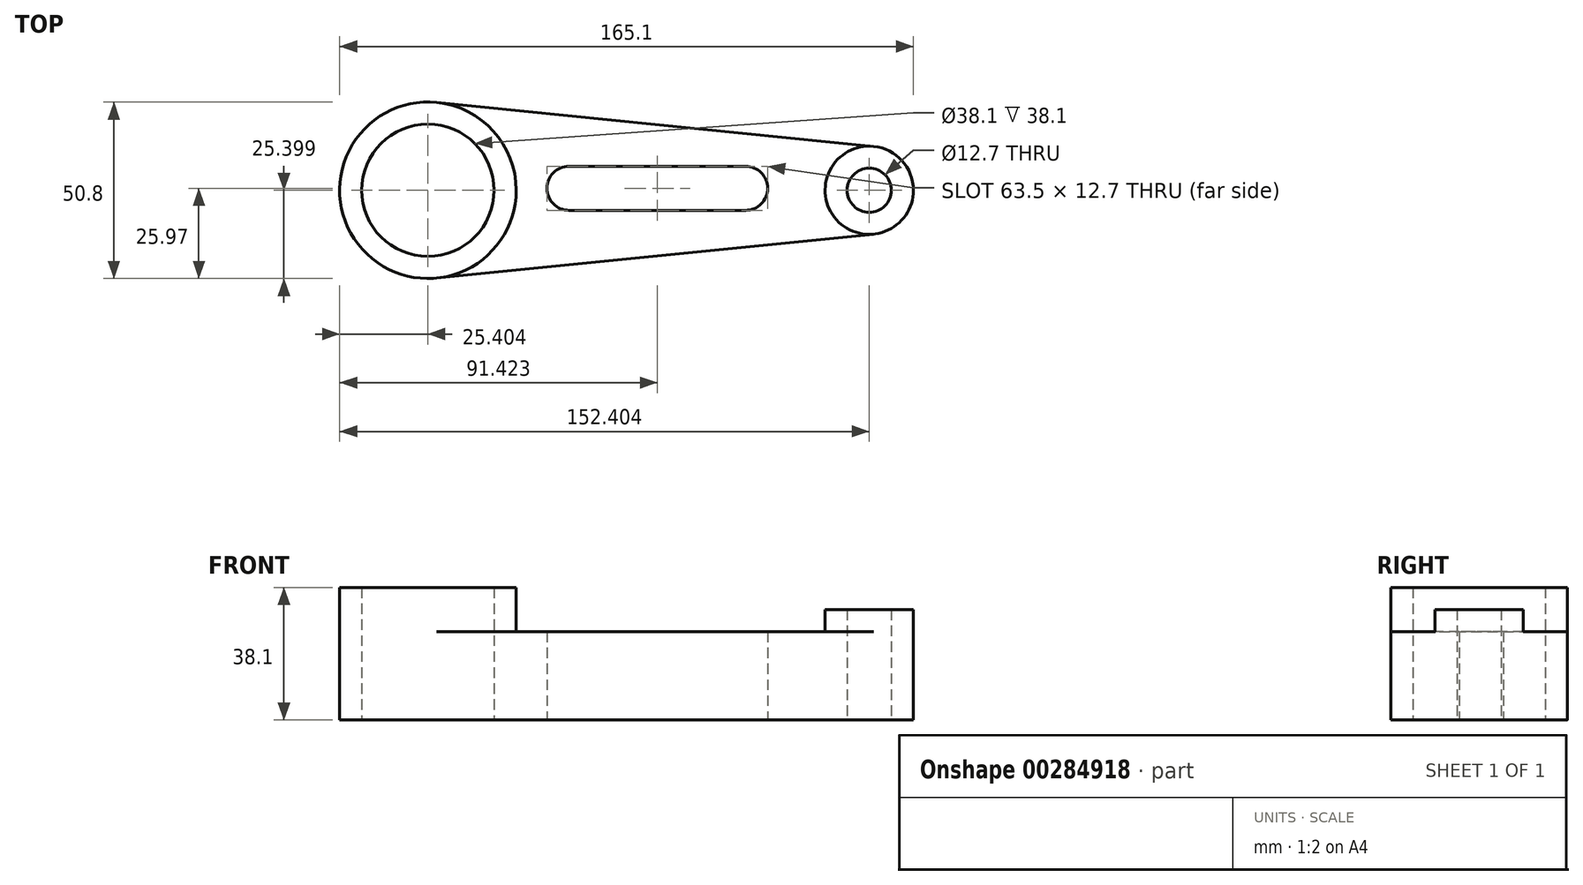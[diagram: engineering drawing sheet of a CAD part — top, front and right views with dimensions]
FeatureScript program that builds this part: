
annotation { "Feature Type Name" : "Feature", "Feature Type Description" : "" }
export const myFeature = defineFeature(function(context is Context, id is Id, definition is map)
    precondition{}
    {
        {
            var Q0;
            Q0=qCreatedBy(makeId("Top.planeOp"),FACE);
            var sketch = newSketch(context, id + "F0", { "sketchPlane" : qUnion([Q0])});
            skCircle(sketch, "E0", {"center": v(-47.88, -0.57) * mm, "radius": 25.4 * mm});
            skCircle(sketch, "E1", {"center": v(-47.88, -0.57) * mm, "radius": 19.05 * mm});
            skCircle(sketch, "E2", {"center": v(79.12, -0.57) * mm, "radius": 6.35 * mm});
            skCircle(sketch, "E3", {"center": v(79.12, -0.57) * mm, "radius": 12.7 * mm});
            skArc(sketch, "E4", {"start": v(-7.26, 6.35) * mm, "mid": v(-13.6, 0) * mm, "end": v(-7.26, -6.35) * mm});
            skArc(sketch, "E5", {"start": v(43.54, -6.35) * mm, "mid": v(49.9, 0) * mm, "end": v(43.54, 6.35) * mm});
            skLineSegment(sketch, "E6", {"start": v(-45.34, 24.7) * mm, "end": v(83.6, 11.74) * mm});
            skLineSegment(sketch, "E7", {"start": v(-47.35, -26.05) * mm, "end": v(81.08, -13.14) * mm});
            skLineSegment(sketch, "E8", {"start": v(-7.26, 6.35) * mm, "end": v(43.54, 6.35) * mm});
            skLineSegment(sketch, "E9", {"start": v(-7.26, -6.35) * mm, "end": v(43.54, -6.35) * mm});
            skSolve(sketch);
        }
        {
            var Q0;
            Q0=makeQuery(id+"F0.imprint","IMPRINT",FACE,{"disambiguationData":[TD([[makeQuery(id+"F0.imprint","IMPRINT",EDGE,{"derivedFrom":sQuery(id+"F0.wireOp",EDGE,"E1")}),-1.0]])]});
            extrude(context, id + "F1", {"entities" : qUnion([Q0]), "depth" : 38.1 * mm});
        }
        {
            var Q0;
            Q0=makeQuery(id+"F0.imprint","IMPRINT",FACE,{"disambiguationData":[TD([[makeQuery(id+"F0.imprint","IMPRINT",EDGE,{"derivedFrom":sQuery(id+"F0.wireOp",EDGE,"E4")}),-1.0]])]});
            extrude(context, id + "F2", {"entities" : qUnion([Q0]), "operationType" : NewBodyOperationType.ADD, "depth" : 25.4 * mm});
        }
        {
            var Q0;
            Q0=makeQuery(id+"F0.imprint","IMPRINT",FACE,{"disambiguationData":[TD([[makeQuery(id+"F0.imprint","IMPRINT",EDGE,{"derivedFrom":sQuery(id+"F0.wireOp",EDGE,"E2")}),-1.0]])]});
            extrude(context, id + "F3", {"entities" : qUnion([Q0]), "operationType" : NewBodyOperationType.ADD, "depth" : 31.75 * mm});
        }
    });
